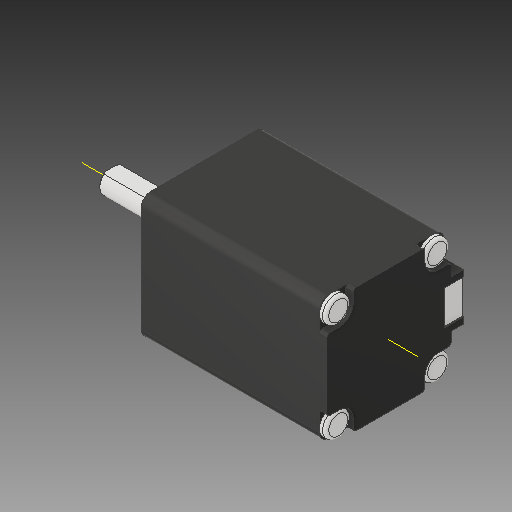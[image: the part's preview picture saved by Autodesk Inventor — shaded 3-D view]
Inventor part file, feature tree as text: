
AUTODESK INVENTOR PART (.ipt)
format: ipt  version: 2019 (Build 230136000, 136)  size: 313,856 bytes
history: native  units: mm
features: sketch x12, other x4
ambient origin geometry x8: Origin, YZ Plane, XZ Plane, XY Plane, X Axis, Y Axis, Z Axis, Center Point
bodies: Solid1 (feature_tree)
feature tree (16):
  other  "Nema-8-stepper-motor.ipt"
  other  "Solid2::Nema-8-stepper-motor.ipt"
  other  "TaggingFeature1"
  sketch  "Sketch1"  dims[d0=10.0mm]
  sketch  "Sketch4"
  sketch  "Sketch5"
  sketch  "Sketch6"
  sketch  "Sketch7"
  sketch  "Sketch8"
  sketch  "Sketch9"
  sketch  "Sketch10"
  sketch  "Sketch12"
  sketch  "Sketch13"
  sketch  "Sketch14"
  sketch  "Sketch15"
  other  "Work Axis1"
